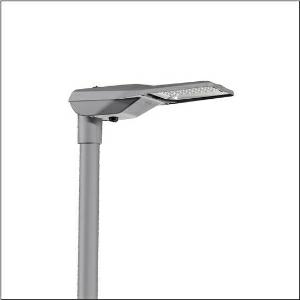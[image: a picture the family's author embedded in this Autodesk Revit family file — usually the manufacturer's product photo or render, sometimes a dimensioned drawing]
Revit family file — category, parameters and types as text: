
# Revit family: streetlight_sl_21_mini___st1_5a_5xe2p43t08hb_3154
name_source: partatom
category: Lighting Fixtures
units: mm (PartAtom-declared; Revit-internal decimal feet)

## family parameters
Cut with Voids When Loaded = No
Host = Face
Light Source = No
Part Type = Normal
Room Calculation Point = No
Round Connector Dimension = Use Diameter
Shared = No

## types (1)
- --- (1 x LED, 9260 lm, 66 W, 4000K)
    Apparent Load = 66 VA
    CIE Flux Codes = 22 53 95 100 100
    Color Rendering = 70
    Color Temperature = 4000K
    Default Elevation = 1800 mm
    Description = Streetlight SL 21 mini, mast luminaire, primary light control with lens, of PMMA, primary optical cover: cover, of toughened safety glass, transparent, light distribution: ST1.5a, light emission: direct distribution, primary light characteristic: asymmetric, installation type: side-entry, post-top, LED, High Power LED, rated luminous flux: 9.260lm, luminous efficacy: 140lm/W, light colour: 740, colour temperature: 4000K, control gear: D4i, control: overheat protection, constant luminous flux control, time-dependent luminous flux control, flexible luminous flux parameterisation, pre-setting: logarithmic dimming characteristic, mains connection: 220..240V, AC, 50/60Hz, start of lifetime: 66W, end of service life: 69W, reduction: 30W, luminaire housing, of diecast aluminium, powder-coated, Siteco® metallic grey (DB 702S), corrosivity category C5 mid according to DIN EN ISO 12944, please order mast flange separately, inclination adjustable: 0°, 5°, 10°, 15°, sealing non-destructively replaceable, multi-level sealing system, length: 628mm, width: 235mm, height: 110mm, mast flange for spigot size: 42mm (side-entry): 5XC10008XM4, 60/48mm (side-entry/post-top): 5XC10108XM2, 76/60mm (side-entry/post-top): 5XC10108XM1, mounting height: 4..8m, Smart Interface below and above, protection rating (complete): IP66, insulation class (complete): insulation class II (safety insulation), certification: CE, ENEC, ENEC+, VDE, impact resistance: IK10, permissible operating ambient temperature for outdoor applications: -40..+50°C, standard-compliant lighting for roads and squares, packaging unit: 1 piece

Light Distribution: ST1.5a
    Height = 110 mm
    Lamp = 1 x LED
    Lamp Light Flux = 9260 lm
    Lamp Power = 66 W
    Lamp count = 1
    Length = 625 mm
    Luminous efficacy = 140 lm/W
    Manufacturer = Siteco
    ModVariant = No
    Model = 5XE2P43T08HB
    Number of Poles = 1
    OnlyDefault = Yes
    Power Factor = 1
    Product Name = Streetlight SL 21 mini | ST1.5a
    Product group = mast luminaire | pylon top
    ProductGroupID = 6100
    Protection Class = Protection class II
    Protection Degree = IP 66
    RLX_Detail_Level = 1
    RLX_Emergency_Light_Flux = 0 lm
    RLX_Emergency_Type = 0
    RLX_Emergency_Type_DB = No
    RlxData = <blob elided: 29777 chars, md5=9463be99>
    Socket = socket
    Standby Power = 0 W
    System Light Flux = 9260 lm
    System Power = 66 W
    Type Comments = factory setting: luminous flux: 100 % | dim-lin: 254 | 670 mA
    Type Image = l_1003514.jpg
    URL = http://relux.com
    VarID = @adj_175456
    Voltage = 0 V
    Weight = 0.00 kg
    Width = 234 mm

## geometry (parser evidence)
native form markers: Blend x4, Sweep x9
no freeform markers — native parametric forms only
